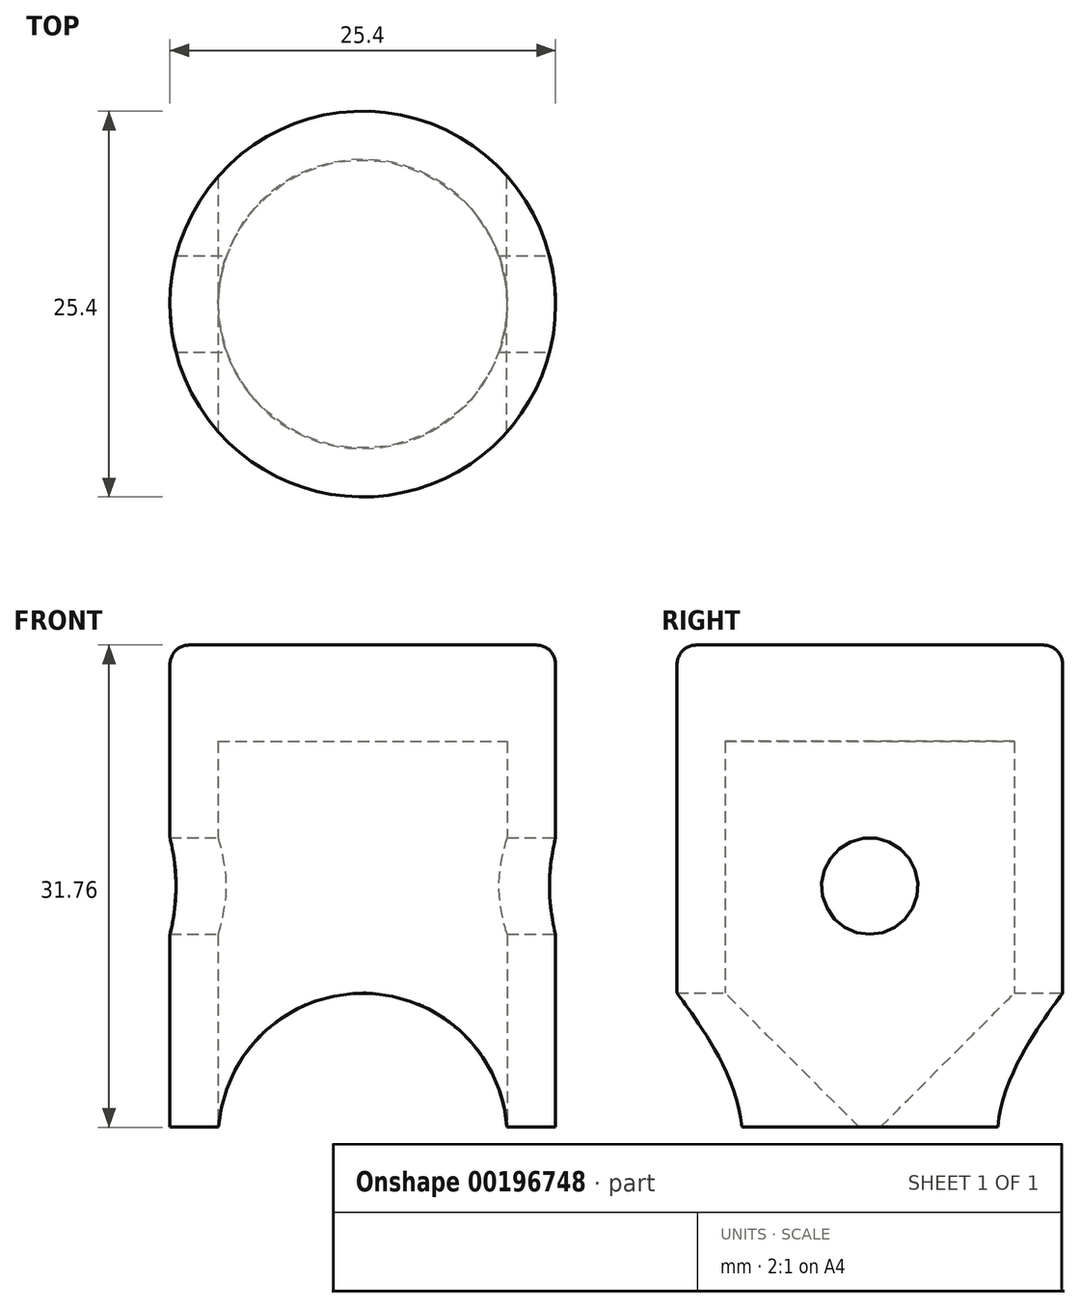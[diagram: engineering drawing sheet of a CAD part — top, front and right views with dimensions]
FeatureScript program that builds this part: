
annotation { "Feature Type Name" : "Feature", "Feature Type Description" : "" }
export const myFeature = defineFeature(function(context is Context, id is Id, definition is map)
    precondition{}
    {
        {
            var Q0;
            Q0=qCreatedBy(makeId("Top.planeOp"),FACE);
            var sketch = newSketch(context, id + "F0", { "sketchPlane" : qUnion([Q0])});
            skCircle(sketch, "E0", {"center": v(0, 0) * mm, "radius": 12.7 * mm});
            skSolve(sketch);
        }
        {
            var Q0;
            Q0=makeQuery(id+"F0.imprint","IMPRINT",FACE,{"disambiguationData":[TD([[makeQuery(id+"F0.imprint","IMPRINT",EDGE,{"derivedFrom":sQuery(id+"F0.wireOp",EDGE,"E0")}),1.0]])]});
            extrude(context, id + "F1", {"entities" : qUnion([Q0]), "depth" : 15.88 * mm, "hasSecondDirection" : true, "secondDirectionOppositeDirection" : true, "secondDirectionDepth" : 15.88 * mm});
        }
        {
            var Q0;
            Q0=makeQuery(id+"F1.opExtrude","CAP_FACE",FACE,{"disambiguationData":[OSD([sQuery(id+"F0.wireOp",EDGE,"E0")])],"isStart":true});
            var sketch = newSketch(context, id + "F2", { "sketchPlane" : qUnion([Q0])});
            skCircle(sketch, "E1", {"center": v(0, 0) * mm, "radius": 9.53 * mm});
            skSolve(sketch);
        }
        {
            var Q0;
            Q0=makeQuery(id+"F2.imprint","IMPRINT",FACE,{"disambiguationData":[TD([[makeQuery(id+"F2.imprint","IMPRINT",EDGE,{"derivedFrom":sQuery(id+"F2.wireOp",EDGE,"E1")}),1.0]])]});
            extrude(context, id + "F3", {"entities" : qUnion([Q0]), "operationType" : NewBodyOperationType.REMOVE, "oppositeDirection" : true, "depth" : 25.4 * mm});
        }
        {
            var Q0;
            Q0=makeQuery(id+"F1.opExtrude","CAP_FACE",FACE,{"disambiguationData":[OSD([sQuery(id+"F0.wireOp",EDGE,"E0")])],"isStart":false});
            fillet(context, id + "F4", {"entities" : qUnion([Q0]), "radius" : 1.27 * mm, "tangentPropagation" : true, "allowEdgeOverflow" : false});
        }
        {
            var Q0;
            Q0=qCreatedBy(makeId("Front.planeOp"),FACE);
            var sketch = newSketch(context, id + "F5", { "sketchPlane" : qUnion([Q0])});
            skLineSegment(sketch, "E2", {"start": v(0, 0) * mm, "end": v(0, -16.57) * mm});
            skCircle(sketch, "E3", {"center": v(0, -16.57) * mm, "radius": 9.53 * mm});
            skSolve(sketch);
        }
        {
            var Q0;
            Q0=makeQuery(id+"F5.imprint","IMPRINT",FACE,{"disambiguationData":[TD([[makeQuery(id+"F5.imprint","IMPRINT",EDGE,{"derivedFrom":sQuery(id+"F5.wireOp",EDGE,"E3")}),1.0]])]});
            extrude(context, id + "F6", {"entities" : qUnion([Q0]), "operationType" : NewBodyOperationType.REMOVE, "depth" : 25.4 * mm, "hasSecondDirection" : true, "secondDirectionOppositeDirection" : true, "secondDirectionDepth" : 25.4 * mm});
        }
        {
            var Q0;
            Q0=qCreatedBy(makeId("Right.planeOp"),FACE);
            var sketch = newSketch(context, id + "F7", { "sketchPlane" : qUnion([Q0])});
            skCircle(sketch, "E4", {"center": v(0, 0) * mm, "radius": 3.18 * mm});
            skSolve(sketch);
        }
        {
            var Q0;
            Q0=makeQuery(id+"F7.imprint","IMPRINT",FACE,{"disambiguationData":[TD([[makeQuery(id+"F7.imprint","IMPRINT",EDGE,{"derivedFrom":sQuery(id+"F7.wireOp",EDGE,"E4")}),1.0]])]});
            extrude(context, id + "F8", {"entities" : qUnion([Q0]), "operationType" : NewBodyOperationType.REMOVE, "oppositeDirection" : true, "depth" : 12.7 * mm, "hasSecondDirection" : true, "secondDirectionOppositeDirection" : false, "secondDirectionDepth" : 12.7 * mm});
        }
    });
